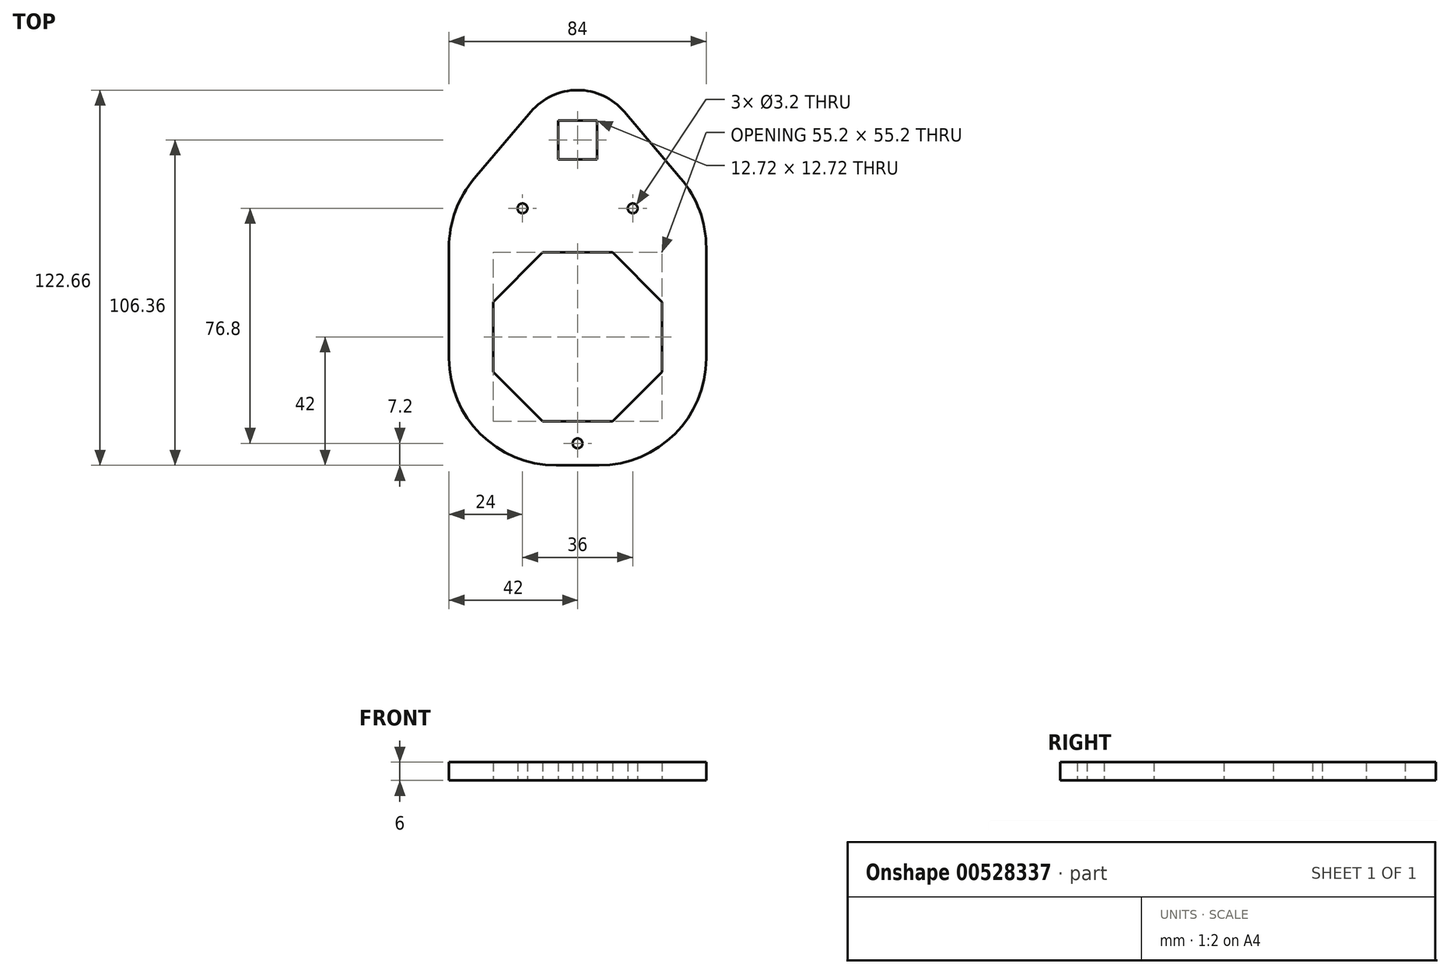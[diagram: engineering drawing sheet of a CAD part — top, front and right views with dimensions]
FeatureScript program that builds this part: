
annotation { "Feature Type Name" : "Feature", "Feature Type Description" : "" }
export const myFeature = defineFeature(function(context is Context, id is Id, definition is map)
    precondition{}
    {
        {
            var Q0;
            Q0=qCreatedBy(makeId("Top.planeOp"),FACE);
            var sketch = newSketch(context, id + "F0", { "sketchPlane" : qUnion([Q0])});
            skLineSegment(sketch, "E0.bottom", {"start": v(0, 0) * mm, "end": v(55.2, 0) * mm});
            skLineSegment(sketch, "E0.top", {"start": v(0, 55.2) * mm, "end": v(55.2, 55.2) * mm, "construction": true});
            skLineSegment(sketch, "E0.left", {"start": v(0, 0) * mm, "end": v(0, 55.2) * mm, "construction": true});
            skLineSegment(sketch, "E0.right", {"start": v(55.2, 0) * mm, "end": v(55.2, 55.2) * mm, "construction": true});
            skLineSegment(sketch, "E1", {"start": v(0, 39.03) * mm, "end": v(16.17, 55.2) * mm});
            skLineSegment(sketch, "E2", {"start": v(39.03, 0) * mm, "end": v(55.2, 16.17) * mm});
            skLineSegment(sketch, "E3", {"start": v(39.03, 55.2) * mm, "end": v(55.2, 39.03) * mm});
            skLineSegment(sketch, "E4", {"start": v(0, 16.17) * mm, "end": v(16.17, 0) * mm});
            skCircle(sketch, "E5", {"center": v(27.6, 27.6) * mm, "radius": 27.6 * mm});
            skPoint(sketch, "E5.centerSnap0", {"position": v(0, 27.6) * mm});
            skPoint(sketch, "E6", {"position": v(27.6, 55.2) * mm});
            skLineSegment(sketch, "E7", {"start": v(-14.4, 69.6) * mm, "end": v(-14.4, -14.4) * mm});
            skLineSegment(sketch, "E8", {"start": v(-14.4, -14.4) * mm, "end": v(69.6, -14.4) * mm});
            skLineSegment(sketch, "E9", {"start": v(69.6, -14.4) * mm, "end": v(69.6, 69.6) * mm});
            skLineSegment(sketch, "E10", {"start": v(69.6, 69.6) * mm, "end": v(-14.4, 69.6) * mm, "construction": true});
            skLineSegment(sketch, "E11", {"start": v(-14.4, 27.6) * mm, "end": v(69.6, 27.6) * mm, "construction": true});
            skLineSegment(sketch, "E12", {"start": v(27.6, -14.4) * mm, "end": v(27.6, 69.6) * mm, "construction": true});
            skLineSegment(sketch, "E13", {"start": v(-14.4, 69.6) * mm, "end": v(27.6, 119.2) * mm});
            skLineSegment(sketch, "E14", {"start": v(69.6, 69.6) * mm, "end": v(27.6, 119.2) * mm});
            skLineSegment(sketch, "E15", {"start": v(0, 39.03) * mm, "end": v(0, 16.17) * mm});
            skLineSegment(sketch, "E16", {"start": v(16.17, 55.2) * mm, "end": v(39.03, 55.2) * mm});
            skLineSegment(sketch, "E17", {"start": v(55.2, 39.03) * mm, "end": v(55.2, 16.17) * mm});
            skLineSegment(sketch, "E18", {"start": v(16.17, 0) * mm, "end": v(39.03, 0) * mm});
            skLineSegment(sketch, "E19.bottom", {"start": v(33.96, 98.32) * mm, "end": v(21.24, 98.32) * mm});
            skLineSegment(sketch, "E19.top", {"start": v(33.96, 85.6) * mm, "end": v(21.24, 85.6) * mm});
            skLineSegment(sketch, "E19.left", {"start": v(33.96, 98.32) * mm, "end": v(33.96, 85.6) * mm});
            skLineSegment(sketch, "E19.right", {"start": v(21.24, 98.32) * mm, "end": v(21.24, 85.6) * mm});
            skLineSegment(sketch, "E20", {"start": v(27.6, 69.6) * mm, "end": v(27.6, 119.2) * mm, "construction": true});
            skPoint(sketch, "E21", {"position": v(27.6, 98.32) * mm});
            skCircle(sketch, "E22", {"center": v(9.6, 69.6) * mm, "radius": 1.6 * mm});
            skCircle(sketch, "E23", {"center": v(45.6, 69.6) * mm, "radius": 1.6 * mm});
            skPoint(sketch, "E24", {"position": v(27.6, 0) * mm});
            skPoint(sketch, "E25", {"position": v(27.6, -7.2) * mm});
            skCircle(sketch, "E26", {"center": v(27.6, -7.2) * mm, "radius": 1.6 * mm});
            skSolve(sketch);
        }
        {
            var Q0;
            Q0=qSketchRegion(id+"F0",true);
            extrude(context, id + "F1", {"entities" : qUnion([Q0]), "depth" : 6 * mm});
        }
        {
            var Q0;
            Q0=makeQuery(id+"F1.opExtrude","SWEPT_EDGE",EDGE,{"disambiguationData":[OSD([sQuery(id+"F0.wireOp",EDGE,"E8"),sQuery(id+"F0.wireOp",EDGE,"E9")])]});
            var Q1;
            Q1=makeQuery(id+"F1.opExtrude","SWEPT_EDGE",EDGE,{"disambiguationData":[OSD([sQuery(id+"F0.wireOp",EDGE,"E7"),sQuery(id+"F0.wireOp",EDGE,"E8")])]});
            var Q2;
            Q2=makeQuery(id+"F1.opExtrude","SWEPT_EDGE",EDGE,{"disambiguationData":[OSD([sQuery(id+"F0.wireOp",EDGE,"E7"),sQuery(id+"F0.wireOp",EDGE,"E10"),sQuery(id+"F0.wireOp",EDGE,"E13")])]});
            var Q3;
            Q3=makeQuery(id+"F1.opExtrude","SWEPT_EDGE",EDGE,{"disambiguationData":[OSD([sQuery(id+"F0.wireOp",EDGE,"E9"),sQuery(id+"F0.wireOp",EDGE,"E10"),sQuery(id+"F0.wireOp",EDGE,"E14")])]});
            fillet(context, id + "F2", {"entities" : qUnion([Q0, Q1, Q2, Q3]), "radius" : 35 * mm, "tangentPropagation" : true, "allowEdgeOverflow" : false});
        }
        {
            var Q0;
            Q0=makeQuery(id+"F1.opExtrude","SWEPT_EDGE",EDGE,{"disambiguationData":[OSD([sQuery(id+"F0.wireOp",EDGE,"E13"),sQuery(id+"F0.wireOp",EDGE,"E14")])]});
            fillet(context, id + "F3", {"entities" : qUnion([Q0]), "radius" : 20 * mm, "tangentPropagation" : true, "allowEdgeOverflow" : false});
        }
    });
